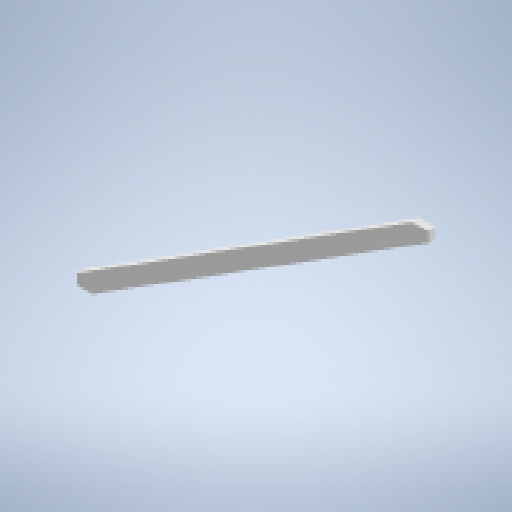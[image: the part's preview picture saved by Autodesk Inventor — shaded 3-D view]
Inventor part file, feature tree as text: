
AUTODESK INVENTOR PART (.ipt)
format: ipt  version: 2025.1 (Build 291241020, 241B)  size: 137,216 bytes
history: native  units: in
note: dims shown in document units (in); Inventor stores cm internally (conversion verified against a paired STEP export)
features: other x6, reference x4, extrude x1, sketch x1
ambient origin geometry x8: Origin, YZ Plane, XZ Plane, XY Plane, X Axis, Y Axis, Z Axis, Center Point
bodies: Solid1 (feature_tree)
feature tree (12):
  extrude  "Extrusion1"  [1 undecoded]
  sketch  "Sketch1"  dims[d2=1.5in d3=0.0in]
  reference  "Reference1"
  reference  "Reference2"
  reference  "Reference3"
  reference  "Reference4"
  other  "<userpath>\Documents\Tburn24\Assembly1.iam"
  other  "Assembly1.iam"
  other  "6'x4x4:22"
  other  "16'x2x4:2"
  other  "16'x4x4:1"
  other  "6'x2x4:1"
note: 1 required parameter value undecoded (feature->parameter linkage not recoverable at this tier; creation-order binding heuristic only, values carry confidence <= 0.55)
